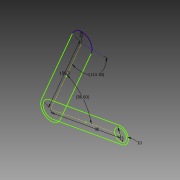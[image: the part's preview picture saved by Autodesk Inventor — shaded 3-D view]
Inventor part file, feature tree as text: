
AUTODESK INVENTOR PART (.ipt)
format: ipt  version: 2020 (Build 240168000, 168)  size: 80,384 bytes
history: native  units: mm
features: sketch x1
ambient origin geometry x8: Origin, YZ Plane, XZ Plane, XY Plane, X Axis, Y Axis, Z Axis, Center Point
feature tree (1):
  sketch  "Sketch1"  dims[d1=100.3mm d12=13.0mm d13=10.0mm d14=15.0mm d15=19.738906mm d16=9.87812mm d17=90.0mm]
